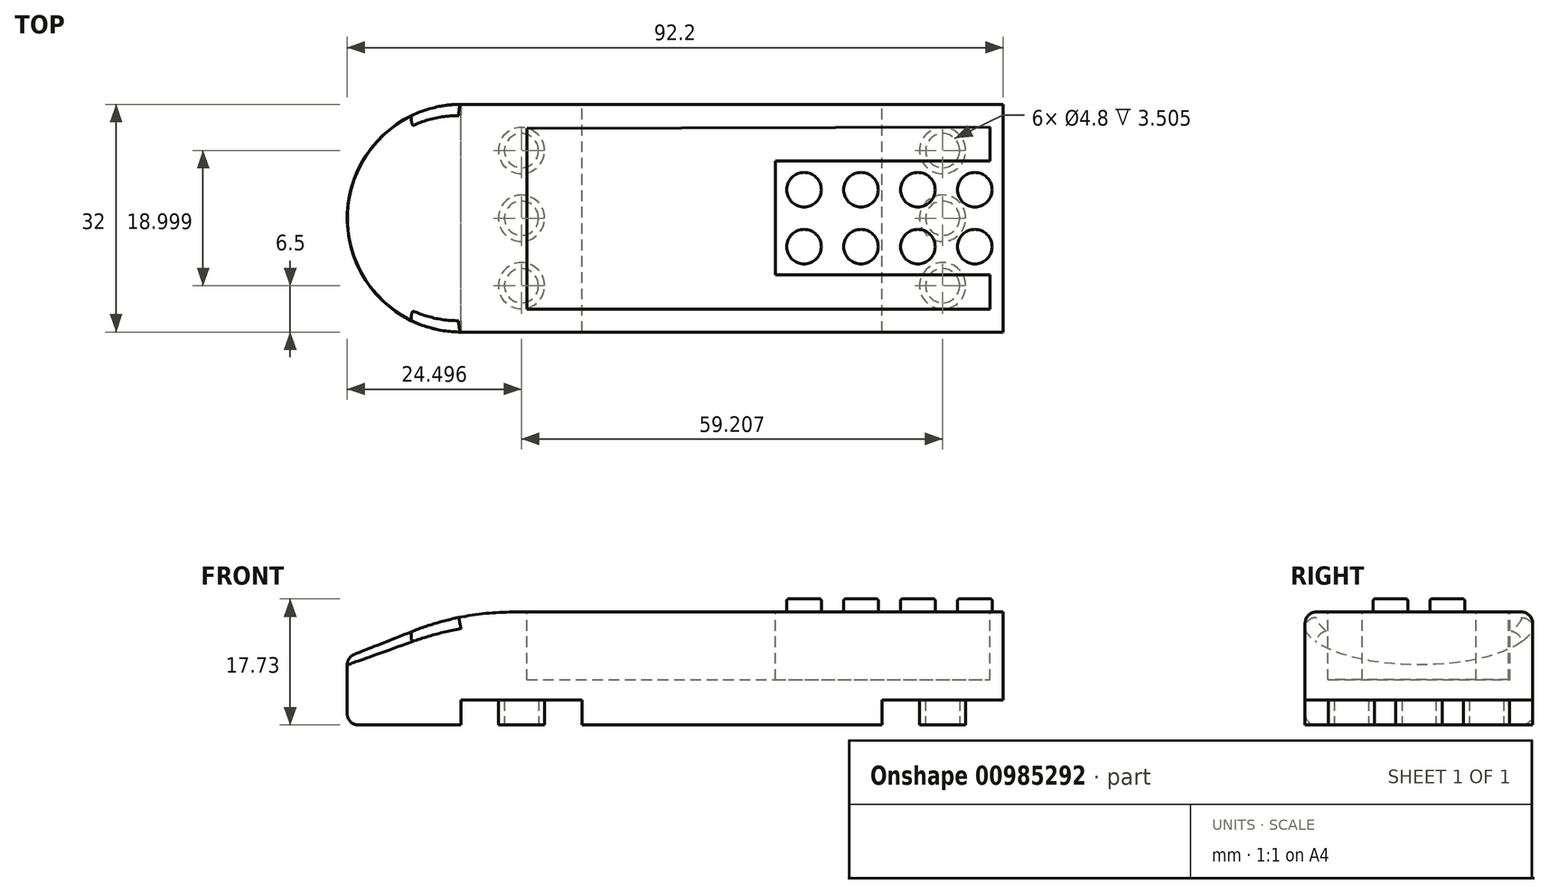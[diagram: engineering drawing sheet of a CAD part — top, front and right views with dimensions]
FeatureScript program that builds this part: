
annotation { "Feature Type Name" : "Feature", "Feature Type Description" : "" }
export const myFeature = defineFeature(function(context is Context, id is Id, definition is map)
    precondition{}
    {
        {
            var Q0;
            Q0=qCreatedBy(makeId("Top.planeOp"),FACE);
            var sketch = newSketch(context, id + "F0", { "sketchPlane" : qUnion([Q0])});
            skLineSegment(sketch, "E0.bottom", {"start": v(-38.1, 16) * mm, "end": v(38.1, 16) * mm});
            skLineSegment(sketch, "E0.top", {"start": v(-38.1, -16) * mm, "end": v(38.1, -16) * mm});
            skLineSegment(sketch, "E0.right", {"start": v(38.1, 16) * mm, "end": v(38.1, -16) * mm});
            skArc(sketch, "E1", {"start": v(-38.1, -16) * mm, "mid": v(-54.1, 0) * mm, "end": v(-38.1, 16) * mm});
            skSolve(sketch);
        }
        {
            var Q0;
            Q0=makeQuery(id+"F0.imprint","IMPRINT",FACE,{"disambiguationData":[TD([[makeQuery(id+"F0.imprint","IMPRINT",EDGE,{"derivedFrom":sQuery(id+"F0.wireOp",EDGE,"E0.bottom")}),-1.0]])]});
            extrude(context, id + "F1", {"entities" : qUnion([Q0]), "depth" : 19.05 * mm, "offsetDistance" : 25.4 * mm});
        }
        {
            var Q0;
            Q0=makeQuery(id+"F1.opExtrude","CAP_FACE",FACE,{"disambiguationData":[OSD([sQuery(id+"F0.wireOp",EDGE,"E0.bottom"),sQuery(id+"F0.wireOp",EDGE,"E0.top"),sQuery(id+"F0.wireOp",EDGE,"E0.left"),sQuery(id+"F0.wireOp",EDGE,"E0.right")])],"isStart":true});
            var sketch = newSketch(context, id + "F2", { "sketchPlane" : qUnion([Q0])});
            skLineSegment(sketch, "E2.bottom", {"start": v(-38.1, 16) * mm, "end": v(-21.1, 16) * mm});
            skLineSegment(sketch, "E2.top", {"start": v(-38.1, -16) * mm, "end": v(-21.1, -16) * mm});
            skLineSegment(sketch, "E2.left", {"start": v(-38.1, 16) * mm, "end": v(-38.1, -16) * mm});
            skLineSegment(sketch, "E2.right", {"start": v(-21.1, 16) * mm, "end": v(-21.1, -16) * mm});
            skLineSegment(sketch, "E3.bottom", {"start": v(38.1, 16) * mm, "end": v(21.1, 16) * mm});
            skLineSegment(sketch, "E3.top", {"start": v(38.1, -16) * mm, "end": v(21.1, -16) * mm});
            skLineSegment(sketch, "E3.left", {"start": v(38.1, 16) * mm, "end": v(38.1, -16) * mm});
            skLineSegment(sketch, "E3.right", {"start": v(21.1, 16) * mm, "end": v(21.1, -16) * mm});
            skCircle(sketch, "E4", {"center": v(-29.6, 9.5) * mm, "radius": 3.25 * mm});
            skCircle(sketch, "E5", {"center": v(-29.6, 9.5) * mm, "radius": 2.4 * mm});
            skCircle(sketch, "E6", {"center": v(-29.6, 0) * mm, "radius": 3.25 * mm});
            skCircle(sketch, "E7", {"center": v(-29.6, -9.5) * mm, "radius": 3.25 * mm});
            skCircle(sketch, "E8", {"center": v(-29.6, -9.5) * mm, "radius": 2.4 * mm});
            skCircle(sketch, "E9", {"center": v(-29.6, 0) * mm, "radius": 2.4 * mm});
            skCircle(sketch, "E10", {"center": v(29.6, 9.5) * mm, "radius": 3.25 * mm});
            skCircle(sketch, "E11", {"center": v(29.6, 9.5) * mm, "radius": 2.4 * mm});
            skCircle(sketch, "E12", {"center": v(29.6, 0) * mm, "radius": 3.25 * mm});
            skCircle(sketch, "E13", {"center": v(29.6, 0) * mm, "radius": 2.4 * mm});
            skCircle(sketch, "E14", {"center": v(29.6, -9.5) * mm, "radius": 3.25 * mm});
            skCircle(sketch, "E15", {"center": v(29.6, -9.5) * mm, "radius": 2.4 * mm});
            skSolve(sketch);
        }
        {
            var Q0;
            Q0 = qSketchRegion(id + "F2", true);
            var Q1;
            Q1=makeQuery(id+"F2.imprint","IMPRINT",FACE,{"disambiguationData":[TD([[makeQuery(id+"F2.imprint","IMPRINT",EDGE,{"derivedFrom":sQuery(id+"F2.wireOp",EDGE,"E5")}),1.0]])]});
            var Q2;
            Q2=makeQuery(id+"F2.imprint","IMPRINT",FACE,{"disambiguationData":[TD([[makeQuery(id+"F2.imprint","IMPRINT",EDGE,{"derivedFrom":sQuery(id+"F2.wireOp",EDGE,"E9")}),1.0]])]});
            var Q3;
            Q3=makeQuery(id+"F2.imprint","IMPRINT",FACE,{"disambiguationData":[TD([[makeQuery(id+"F2.imprint","IMPRINT",EDGE,{"derivedFrom":sQuery(id+"F2.wireOp",EDGE,"E8")}),1.0]])]});
            var Q4;
            Q4=makeQuery(id+"F2.imprint","IMPRINT",FACE,{"disambiguationData":[TD([[makeQuery(id+"F2.imprint","IMPRINT",EDGE,{"derivedFrom":sQuery(id+"F2.wireOp",EDGE,"E11")}),1.0]])]});
            var Q5;
            Q5=makeQuery(id+"F2.imprint","IMPRINT",FACE,{"disambiguationData":[TD([[makeQuery(id+"F2.imprint","IMPRINT",EDGE,{"derivedFrom":sQuery(id+"F2.wireOp",EDGE,"E13")}),1.0]])]});
            var Q6;
            Q6=makeQuery(id+"F2.imprint","IMPRINT",FACE,{"disambiguationData":[TD([[makeQuery(id+"F2.imprint","IMPRINT",EDGE,{"derivedFrom":sQuery(id+"F2.wireOp",EDGE,"E15")}),1.0]])]});
            extrude(context, id + "F3", {"entities" : qUnion([Q0, Q1, Q2, Q3, Q4, Q5, Q6]), "operationType" : NewBodyOperationType.REMOVE, "oppositeDirection" : true, "depth" : 3.5 * mm, "offsetDistance" : 25.4 * mm});
        }
        {
            var Q0;
            Q0=makeQuery(id+"F1.opExtrude","SWEPT_FACE",FACE,{"disambiguationData":[OSD([sQuery(id+"F0.wireOp",EDGE,"E0.top")])]});
            var sketch = newSketch(context, id + "F4", { "sketchPlane" : qUnion([Q0])});
            skLineSegment(sketch, "E16", {"start": v(-54.1, 0) * mm, "end": v(-54.1, 19.05) * mm, "construction": true});
            skLineSegment(sketch, "E17.0", {"start": v(-38.1, 19.05) * mm, "end": v(-54.1, 19.05) * mm, "construction": true});
            skLineSegment(sketch, "E18.0", {"start": v(-38.1, 0) * mm, "end": v(-54.1, 0) * mm, "construction": true});
            skLineSegment(sketch, "E19", {"start": v(-54.1, 9.52) * mm, "end": v(-44.87, 13.19) * mm});
            skLineSegment(sketch, "E20", {"start": v(-30.82, 15.87) * mm, "end": v(38.1, 15.88) * mm});
            skLineSegment(sketch, "E21", {"start": v(38.1, 15.88) * mm, "end": v(38.1, 19.05) * mm});
            skLineSegment(sketch, "E22", {"start": v(38.1, 19.05) * mm, "end": v(-54.1, 19.05) * mm});
            skLineSegment(sketch, "E23", {"start": v(-54.1, 19.05) * mm, "end": v(-54.1, 9.53) * mm});
            skPoint(sketch, "E24.visualSharp", {"position": v(-38.1, 15.87) * mm});
            skArc(sketch, "E24.filletArc", {"start": v(-30.82, 15.87) * mm, "mid": v(-37.97, 15.2) * mm, "end": v(-44.87, 13.19) * mm});
            skSolve(sketch);
        }
        {
            var Q0;
            {var subQ5=sQuery(id+"F4.wireOp",EDGE,"E20");Q0=makeQuery(id+"F4.imprint","IMPRINT",FACE,{"disambiguationData":[TD([[makeQuery(id+"F4.imprint","IMPRINT",EDGE,{"derivedFrom":subQ5}),1.0]])]});}
            var Q1;
            {var subQ1=sQuery(id+"F4.wireOp",EDGE,"E19");Q1=makeQuery(id+"F4.imprint","IMPRINT",FACE,{"disambiguationData":[TD([[makeQuery(id+"F4.imprint","IMPRINT",EDGE,{"derivedFrom":subQ1}),1.0]])]});}
            extrude(context, id + "F5", {"entities" : qUnion([Q0, Q1]), "operationType" : NewBodyOperationType.REMOVE, "endBound" : BoundingType.THROUGH_ALL, "oppositeDirection" : true, "depth" : 25.4 * mm, "offsetDistance" : 25.4 * mm});
        }
        {
            var Q0;
            Q0=makeQuery(id+"F5.boolean.opBoolean","INTERSECT",EDGE,{"derivedFrom":[makeQuery(id+"F1.opExtrude","SWEPT_FACE",FACE,{"disambiguationData":[OSD([sQuery(id+"F0.wireOp",EDGE,"E1")])]}),makeQuery(id+"F5.opExtrude","SWEPT_FACE",FACE,{"disambiguationData":[OSD([sQuery(id+"F4.wireOp",EDGE,"E19")])]})]});
            var Q1;
            Q1=makeQuery(id+"F1.opExtrude","CAP_EDGE",EDGE,{"disambiguationData":[OSD([sQuery(id+"F0.wireOp",EDGE,"E1")])],"isStart":true});
            fillet(context, id + "F6", {"entities" : qUnion([Q0, Q1]), "radius" : 1.59 * mm, "tangentPropagation" : true, "allowEdgeOverflow" : false});
        }
        {
            var Q0;
            Q0=makeQuery(id+"F5.boolean.opBoolean","COPY",FACE,{"derivedFrom":makeQuery(id+"F5.opExtrude","SWEPT_FACE",FACE,{"disambiguationData":[OSD([sQuery(id+"F4.wireOp",EDGE,"E20")])]})});
            var sketch = newSketch(context, id + "F7", { "sketchPlane" : qUnion([Q0])});
            skCircle(sketch, "E25", {"center": v(10.12, 4) * mm, "radius": 2.42 * mm});
            skCircle(sketch, "E26.0.1.0", {"center": v(10.12, -4) * mm, "radius": 2.42 * mm});
            skCircle(sketch, "E26.1.0.0", {"center": v(18.12, 4) * mm, "radius": 2.42 * mm});
            skCircle(sketch, "E26.1.1.0", {"center": v(18.12, -4) * mm, "radius": 2.42 * mm});
            skCircle(sketch, "E26.2.0.0", {"center": v(26.13, 4) * mm, "radius": 2.42 * mm});
            skCircle(sketch, "E26.2.1.0", {"center": v(26.13, -4) * mm, "radius": 2.42 * mm});
            skCircle(sketch, "E26.3.0.0", {"center": v(34.13, 4) * mm, "radius": 2.42 * mm});
            skCircle(sketch, "E26.3.1.0", {"center": v(34.13, -4) * mm, "radius": 2.42 * mm});
            skLineSegment(sketch, "E26.direction1", {"start": v(-4, 11.24) * mm, "end": v(4, 11.24) * mm, "construction": true});
            skLineSegment(sketch, "E26.direction2", {"start": v(-4, 11.24) * mm, "end": v(-4, 3.24) * mm, "construction": true});
            skSolve(sketch);
        }
        {
            var Q0;
            Q0=makeQuery(id+"F7.imprint","IMPRINT",FACE,{"disambiguationData":[TD([[makeQuery(id+"F7.imprint","IMPRINT",EDGE,{"derivedFrom":sQuery(id+"F7.wireOp",EDGE,"E25")}),1.0]])]});
            var Q1;
            Q1=makeQuery(id+"F7.imprint","IMPRINT",FACE,{"disambiguationData":[TD([[makeQuery(id+"F7.imprint","IMPRINT",EDGE,{"derivedFrom":sQuery(id+"F7.wireOp",EDGE,"E26.1.0.0")}),1.0]])]});
            var Q2;
            Q2=makeQuery(id+"F7.imprint","IMPRINT",FACE,{"disambiguationData":[TD([[makeQuery(id+"F7.imprint","IMPRINT",EDGE,{"derivedFrom":sQuery(id+"F7.wireOp",EDGE,"E26.2.0.0")}),1.0]])]});
            var Q3;
            Q3=makeQuery(id+"F7.imprint","IMPRINT",FACE,{"disambiguationData":[TD([[makeQuery(id+"F7.imprint","IMPRINT",EDGE,{"derivedFrom":sQuery(id+"F7.wireOp",EDGE,"E26.3.0.0")}),1.0]])]});
            var Q4;
            Q4=makeQuery(id+"F7.imprint","IMPRINT",FACE,{"disambiguationData":[TD([[makeQuery(id+"F7.imprint","IMPRINT",EDGE,{"derivedFrom":sQuery(id+"F7.wireOp",EDGE,"E26.3.1.0")}),1.0]])]});
            var Q5;
            Q5=makeQuery(id+"F7.imprint","IMPRINT",FACE,{"disambiguationData":[TD([[makeQuery(id+"F7.imprint","IMPRINT",EDGE,{"derivedFrom":sQuery(id+"F7.wireOp",EDGE,"E26.2.1.0")}),1.0]])]});
            var Q6;
            Q6=makeQuery(id+"F7.imprint","IMPRINT",FACE,{"disambiguationData":[TD([[makeQuery(id+"F7.imprint","IMPRINT",EDGE,{"derivedFrom":sQuery(id+"F7.wireOp",EDGE,"E26.1.1.0")}),1.0]])]});
            var Q7;
            Q7=makeQuery(id+"F7.imprint","IMPRINT",FACE,{"disambiguationData":[TD([[makeQuery(id+"F7.imprint","IMPRINT",EDGE,{"derivedFrom":sQuery(id+"F7.wireOp",EDGE,"E26.0.1.0")}),1.0]])]});
            extrude(context, id + "F8", {"entities" : qUnion([Q0, Q1, Q2, Q3, Q4, Q5, Q6, Q7]), "operationType" : NewBodyOperationType.ADD, "depth" : 1.85 * mm, "offsetDistance" : 25.4 * mm});
        }
        {
            var Q0;
            Q0=makeQuery(id+"F8.opExtrude","CAP_EDGE",EDGE,{"disambiguationData":[OSD([sQuery(id+"F7.wireOp",EDGE,"E26.0.1.0")])],"isStart":false});
            var Q1;
            Q1=makeQuery(id+"F8.opExtrude","CAP_EDGE",EDGE,{"disambiguationData":[OSD([sQuery(id+"F7.wireOp",EDGE,"E25")])],"isStart":false});
            var Q2;
            Q2=makeQuery(id+"F8.opExtrude","CAP_EDGE",EDGE,{"disambiguationData":[OSD([sQuery(id+"F7.wireOp",EDGE,"E26.1.0.0")])],"isStart":false});
            var Q3;
            Q3=makeQuery(id+"F8.opExtrude","CAP_EDGE",EDGE,{"disambiguationData":[OSD([sQuery(id+"F7.wireOp",EDGE,"E26.1.1.0")])],"isStart":false});
            var Q4;
            Q4=makeQuery(id+"F8.opExtrude","CAP_EDGE",EDGE,{"disambiguationData":[OSD([sQuery(id+"F7.wireOp",EDGE,"E26.2.0.0")])],"isStart":false});
            var Q5;
            Q5=makeQuery(id+"F8.opExtrude","CAP_EDGE",EDGE,{"disambiguationData":[OSD([sQuery(id+"F7.wireOp",EDGE,"E26.2.1.0")])],"isStart":false});
            var Q6;
            Q6=makeQuery(id+"F8.opExtrude","CAP_EDGE",EDGE,{"disambiguationData":[OSD([sQuery(id+"F7.wireOp",EDGE,"E26.3.1.0")])],"isStart":false});
            var Q7;
            Q7=makeQuery(id+"F8.opExtrude","CAP_EDGE",EDGE,{"disambiguationData":[OSD([sQuery(id+"F7.wireOp",EDGE,"E26.3.0.0")])],"isStart":false});
            fillet(context, id + "F9", {"entities" : qUnion([Q0, Q1, Q2, Q3, Q4, Q5, Q6, Q7]), "radius" : 0.25 * mm, "tangentPropagation" : true, "allowEdgeOverflow" : false});
        }
        {
            var Q0;
            Q0=makeQuery(id+"F5.boolean.opBoolean","COPY",FACE,{"derivedFrom":makeQuery(id+"F5.opExtrude","SWEPT_FACE",FACE,{"disambiguationData":[OSD([sQuery(id+"F4.wireOp",EDGE,"E20")])]})});
            var sketch = newSketch(context, id + "F10", { "sketchPlane" : qUnion([Q0])});
            skLineSegment(sketch, "E27", {"start": v(36.23, 12.78) * mm, "end": v(36.23, 8.02) * mm});
            skLineSegment(sketch, "E28", {"start": v(36.23, 8.02) * mm, "end": v(6.07, 8.02) * mm});
            skLineSegment(sketch, "E29", {"start": v(6.07, 8.02) * mm, "end": v(6.07, -7.99) * mm});
            skLineSegment(sketch, "E30", {"start": v(6.07, -7.99) * mm, "end": v(36.23, -7.99) * mm});
            skLineSegment(sketch, "E31", {"start": v(36.23, -7.99) * mm, "end": v(36.23, -12.76) * mm});
            skLineSegment(sketch, "E32", {"start": v(36.23, -12.76) * mm, "end": v(-28.85, -12.76) * mm});
            skLineSegment(sketch, "E33", {"start": v(-28.85, -12.76) * mm, "end": v(-28.85, 12.64) * mm});
            skLineSegment(sketch, "E34", {"start": v(-28.85, 12.64) * mm, "end": v(36.23, 12.78) * mm});
            skSolve(sketch);
        }
        {
            var Q0;
            Q0=makeQuery(id+"F10.imprint","IMPRINT",FACE,{"disambiguationData":[TD([[makeQuery(id+"F10.imprint","IMPRINT",EDGE,{"derivedFrom":sQuery(id+"F10.wireOp",EDGE,"E27")}),-1.0]])]});
            extrude(context, id + "F11", {"entities" : qUnion([Q0]), "operationType" : NewBodyOperationType.REMOVE, "oppositeDirection" : true, "depth" : 9.52 * mm, "offsetDistance" : 25.4 * mm});
        }
    });
